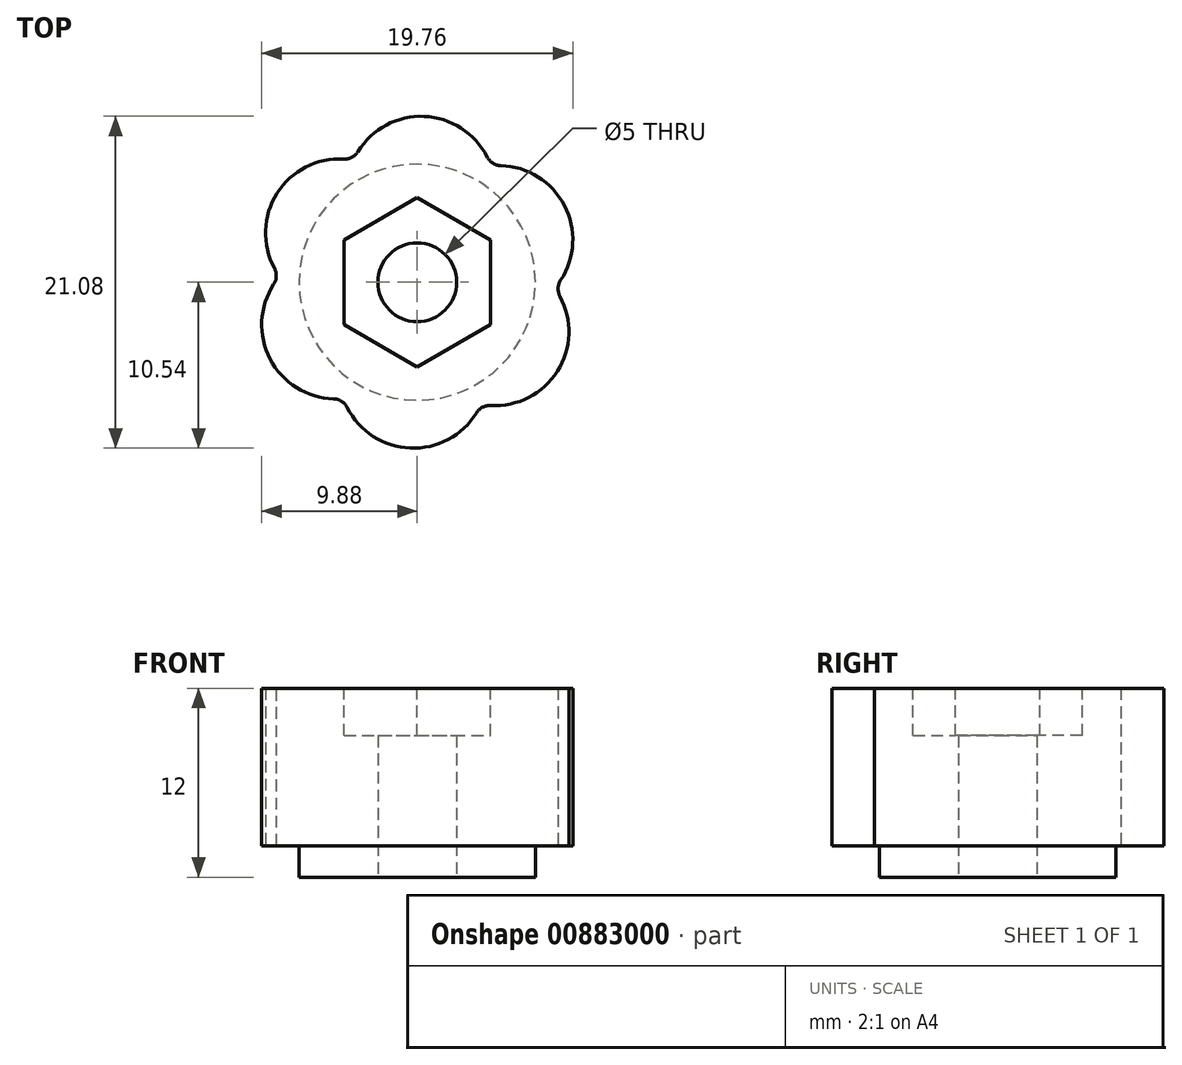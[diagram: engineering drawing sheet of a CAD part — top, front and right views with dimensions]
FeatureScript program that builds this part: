
annotation { "Feature Type Name" : "Feature", "Feature Type Description" : "" }
export const myFeature = defineFeature(function(context is Context, id is Id, definition is map)
    precondition{}
    {
        {
            var Q0;
            Q0=qCreatedBy(makeId("Top.planeOp"),FACE);
            var sketch = newSketch(context, id + "F0", { "sketchPlane" : qUnion([Q0])});
            skCircle(sketch, "E0", {"center": v(0, 0) * mm, "radius": 7.5 * mm});
            skCircle(sketch, "E1", {"center": v(0, 0) * mm, "radius": 3.75 * mm});
            skArc(sketch, "E2", {"start": v(-7.36, 1.46) * mm, "mid": v(-9.35, -4.88) * mm, "end": v(-3, -6.87) * mm});
            skSolve(sketch);
        }
        {
            var Q0;
            Q0=makeQuery(id+"F0.imprint","IMPRINT",FACE,{"disambiguationData":[TD([[makeQuery(id+"F0.imprint","IMPRINT",EDGE,{"derivedFrom":sQuery(id+"F0.wireOp",EDGE,"E0")}),1.0]])]});
            var Q1;
            Q1=makeQuery(id+"F0.imprint","IMPRINT",FACE,{"disambiguationData":[TD([[makeQuery(id+"F0.imprint","IMPRINT",EDGE,{"derivedFrom":sQuery(id+"F0.wireOp",EDGE,"E1")}),1.0]])]});
            extrude(context, id + "F1", {"entities" : qUnion([Q0, Q1]), "depth" : 10 * mm, "offsetDistance" : 25 * mm});
        }
        {
            var Q0;
            Q0=makeQuery(id+"F1.opExtrude","CAP_FACE",FACE,{"disambiguationData":[OSD([sQuery(id+"F0.wireOp",EDGE,"E0")])],"isStart":true});
            var sketch = newSketch(context, id + "F2", { "sketchPlane" : qUnion([Q0])});
            skCircle(sketch, "E3", {"center": v(0, 0) * mm, "radius": 2.5 * mm});
            skSolve(sketch);
        }
        {
            var Q0;
            Q0 = qSketchRegion(id + "F2", true);
            extrude(context, id + "F3", {"entities" : qUnion([Q0]), "operationType" : NewBodyOperationType.REMOVE, "oppositeDirection" : true, "depth" : 7 * mm, "offsetDistance" : 25 * mm});
        }
        {
            var Q0;
            Q0=makeQuery(id+"F1.opExtrude","CAP_FACE",FACE,{"disambiguationData":[OSD([sQuery(id+"F0.wireOp",EDGE,"E0")])],"isStart":true});
            extrude(context, id + "F4", {"entities" : qUnion([Q0]), "operationType" : NewBodyOperationType.ADD, "depth" : 2 * mm, "offsetDistance" : 25 * mm});
        }
        {
            var Q0;
            Q0 = qSketchRegion(id + "F0", true);
            extrude(context, id + "F5", {"entities" : qUnion([Q0]), "depth" : 10 * mm, "offsetDistance" : 25 * mm});
        }
        {
            var Q0;
            Q0=makeQuery(id+"F5.opExtrude","SWEPT_BODY",BODY,{"disambiguationData":[OSD([sQuery(id+"F0.wireOp",EDGE,"E0"),sQuery(id+"F0.wireOp",EDGE,"E1"),sQuery(id+"F0.wireOp",EDGE,"E2")])]});
            var Q1;
            Q1=makeQuery(id+"F5.opExtrude","SWEPT_FACE",FACE,{"disambiguationData":[OSD([sQuery(id+"F0.wireOp",EDGE,"E0")])]});
            circularPattern(context, id + "F6", {"entities" : qUnion([Q0]), "axis" : qUnion([Q1]), "angle" : 360 * degree, "instanceCount" : 6, "equalSpace" : true});
        }
        {
            var Q0;
            Q0=makeQuery(id+"F1.opExtrude","CAP_FACE",FACE,{"disambiguationData":[OSD([sQuery(id+"F0.wireOp",EDGE,"E0")])],"isStart":false});
            var sketch = newSketch(context, id + "F7", { "sketchPlane" : qUnion([Q0])});
            skCircle(sketch, "E4.cCircle", {"center": v(0, 0) * mm, "radius": 4.65 * mm, "construction": true});
            skLineSegment(sketch, "E4.0", {"start": v(4.65, 2.68) * mm, "end": v(4.65, -2.68) * mm});
            skLineSegment(sketch, "E4.1", {"start": v(4.65, -2.68) * mm, "end": v(0, -5.37) * mm});
            skLineSegment(sketch, "E4.2", {"start": v(0, -5.37) * mm, "end": v(-4.65, -2.68) * mm});
            skLineSegment(sketch, "E4.3", {"start": v(-4.65, -2.68) * mm, "end": v(-4.65, 2.68) * mm});
            skLineSegment(sketch, "E4.4", {"start": v(-4.65, 2.68) * mm, "end": v(0, 5.37) * mm});
            skLineSegment(sketch, "E4.5", {"start": v(0, 5.37) * mm, "end": v(4.65, 2.68) * mm});
            skPoint(sketch, "E4.0.midPoint", {"position": v(4.65, 0) * mm});
            skSolve(sketch);
        }
        {
            var Q0;
            Q0 = qSketchRegion(id + "F7", true);
            extrude(context, id + "F8", {"entities" : qUnion([Q0]), "operationType" : NewBodyOperationType.REMOVE, "oppositeDirection" : true, "depth" : 3 * mm, "offsetDistance" : 25 * mm});
        }
        {
            var Q0;
            Q0=makeQuery(id+"F6.opPattern","COPY",BODY,{"derivedFrom":makeQuery(id+"F5.opExtrude","SWEPT_BODY",BODY,{"disambiguationData":[OSD([sQuery(id+"F0.wireOp",EDGE,"E0"),sQuery(id+"F0.wireOp",EDGE,"E1"),sQuery(id+"F0.wireOp",EDGE,"E2")])]}),"instanceName":"1"});
            var Q1;
            Q1=makeQuery(id+"F6.opPattern","COPY",BODY,{"derivedFrom":makeQuery(id+"F5.opExtrude","SWEPT_BODY",BODY,{"disambiguationData":[OSD([sQuery(id+"F0.wireOp",EDGE,"E0"),sQuery(id+"F0.wireOp",EDGE,"E1"),sQuery(id+"F0.wireOp",EDGE,"E2")])]}),"instanceName":"2"});
            var Q2;
            Q2=makeQuery(id+"F5.opExtrude","SWEPT_BODY",BODY,{"disambiguationData":[OSD([sQuery(id+"F0.wireOp",EDGE,"E0"),sQuery(id+"F0.wireOp",EDGE,"E1"),sQuery(id+"F0.wireOp",EDGE,"E2")])]});
            var Q3;
            Q3=makeQuery(id+"F6.opPattern","COPY",BODY,{"derivedFrom":makeQuery(id+"F5.opExtrude","SWEPT_BODY",BODY,{"disambiguationData":[OSD([sQuery(id+"F0.wireOp",EDGE,"E0"),sQuery(id+"F0.wireOp",EDGE,"E1"),sQuery(id+"F0.wireOp",EDGE,"E2")])]}),"instanceName":"3"});
            var Q4;
            Q4=makeQuery(id+"F1.opExtrude","SWEPT_BODY",BODY,{"disambiguationData":[OSD([sQuery(id+"F0.wireOp",EDGE,"E0")])]});
            var Q5;
            Q5=makeQuery(id+"F6.opPattern","COPY",BODY,{"derivedFrom":makeQuery(id+"F5.opExtrude","SWEPT_BODY",BODY,{"disambiguationData":[OSD([sQuery(id+"F0.wireOp",EDGE,"E0"),sQuery(id+"F0.wireOp",EDGE,"E1"),sQuery(id+"F0.wireOp",EDGE,"E2")])]}),"instanceName":"5"});
            var Q6;
            Q6=makeQuery(id+"F6.opPattern","COPY",BODY,{"derivedFrom":makeQuery(id+"F5.opExtrude","SWEPT_BODY",BODY,{"disambiguationData":[OSD([sQuery(id+"F0.wireOp",EDGE,"E0"),sQuery(id+"F0.wireOp",EDGE,"E1"),sQuery(id+"F0.wireOp",EDGE,"E2")])]}),"instanceName":"4"});
            booleanBodies(context, id + "F9", {"operationType" : BooleanOperationType.UNION, "tools" : qUnion([Q0, Q1, Q2, Q3, Q4, Q5, Q6])});
        }
        {
            var Q0;
            {var subQ0=makeQuery(id+"F5.opExtrude","SWEPT_FACE",FACE,{"disambiguationData":[OSD([sQuery(id+"F0.wireOp",EDGE,"E2")])]});Q0=makeQuery(id+"F9.opBoolean","INTERSECT",EDGE,{"derivedFrom":[subQ0,makeQuery(id+"F6.opPattern","COPY",FACE,{"derivedFrom":subQ0,"instanceName":"5"})]});}
            var Q1;
            {var subQ0=makeQuery(id+"F5.opExtrude","SWEPT_FACE",FACE,{"disambiguationData":[OSD([sQuery(id+"F0.wireOp",EDGE,"E2")])]});Q1=makeQuery(id+"F9.opBoolean","INTERSECT",EDGE,{"derivedFrom":[makeQuery(id+"F6.opPattern","COPY",FACE,{"derivedFrom":subQ0,"instanceName":"4"}),makeQuery(id+"F6.opPattern","COPY",FACE,{"derivedFrom":subQ0,"instanceName":"5"})]});}
            var Q2;
            {var subQ0=makeQuery(id+"F5.opExtrude","SWEPT_FACE",FACE,{"disambiguationData":[OSD([sQuery(id+"F0.wireOp",EDGE,"E2")])]});Q2=makeQuery(id+"F9.opBoolean","INTERSECT",EDGE,{"derivedFrom":[makeQuery(id+"F6.opPattern","COPY",FACE,{"derivedFrom":subQ0,"instanceName":"3"}),makeQuery(id+"F6.opPattern","COPY",FACE,{"derivedFrom":subQ0,"instanceName":"4"})]});}
            var Q3;
            {var subQ0=makeQuery(id+"F5.opExtrude","SWEPT_FACE",FACE,{"disambiguationData":[OSD([sQuery(id+"F0.wireOp",EDGE,"E2")])]});Q3=makeQuery(id+"F9.opBoolean","INTERSECT",EDGE,{"derivedFrom":[makeQuery(id+"F6.opPattern","COPY",FACE,{"derivedFrom":subQ0,"instanceName":"2"}),makeQuery(id+"F6.opPattern","COPY",FACE,{"derivedFrom":subQ0,"instanceName":"3"})]});}
            var Q4;
            {var subQ0=makeQuery(id+"F5.opExtrude","SWEPT_FACE",FACE,{"disambiguationData":[OSD([sQuery(id+"F0.wireOp",EDGE,"E2")])]});Q4=makeQuery(id+"F9.opBoolean","INTERSECT",EDGE,{"derivedFrom":[makeQuery(id+"F6.opPattern","COPY",FACE,{"derivedFrom":subQ0,"instanceName":"1"}),makeQuery(id+"F6.opPattern","COPY",FACE,{"derivedFrom":subQ0,"instanceName":"2"})]});}
            var Q5;
            {var subQ0=makeQuery(id+"F5.opExtrude","SWEPT_FACE",FACE,{"disambiguationData":[OSD([sQuery(id+"F0.wireOp",EDGE,"E2")])]});Q5=makeQuery(id+"F9.opBoolean","INTERSECT",EDGE,{"derivedFrom":[subQ0,makeQuery(id+"F6.opPattern","COPY",FACE,{"derivedFrom":subQ0,"instanceName":"1"})]});}
            fillet(context, id + "F10", {"entities" : qUnion([Q0, Q1, Q2, Q3, Q4, Q5]), "radius" : 1 * mm, "tangentPropagation" : true, "allowEdgeOverflow" : false});
        }
    });
